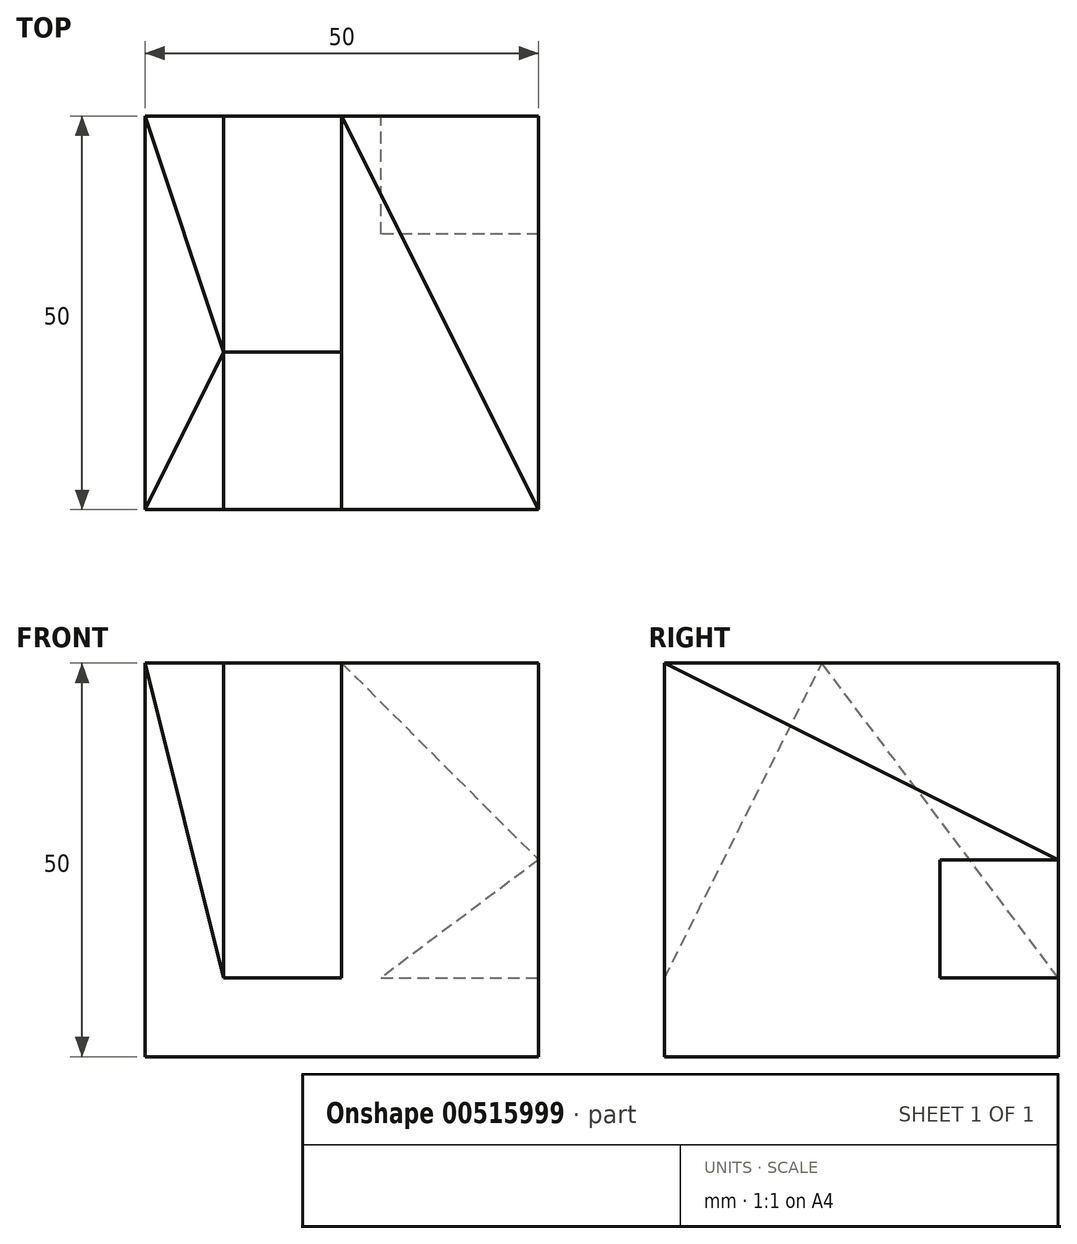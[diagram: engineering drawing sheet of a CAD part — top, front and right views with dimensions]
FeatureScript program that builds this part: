
annotation { "Feature Type Name" : "Feature", "Feature Type Description" : "" }
export const myFeature = defineFeature(function(context is Context, id is Id, definition is map)
    precondition{}
    {
        {
            var Q0;
            Q0=qCreatedBy(makeId("Front.planeOp"),FACE);
            var sketch = newSketch(context, id + "F0", { "sketchPlane" : qUnion([Q0])});
            skLineSegment(sketch, "E0.bottom", {"start": v(0, 0) * mm, "end": v(50, 0) * mm});
            skLineSegment(sketch, "E0.top", {"start": v(0, 50) * mm, "end": v(50, 50) * mm});
            skLineSegment(sketch, "E0.left", {"start": v(0, 0) * mm, "end": v(0, 50) * mm});
            skLineSegment(sketch, "E0.right", {"start": v(50, 0) * mm, "end": v(50, 50) * mm});
            skSolve(sketch);
        }
        {
            var Q0;
            Q0 = qSketchRegion(id + "F0", true);
            extrude(context, id + "F1", {"entities" : qUnion([Q0]), "depth" : 50 * mm, "offsetDistance" : 25 * mm});
        }
        {
            var Q0;
            Q0=makeQuery(id+"F1.opExtrude","SWEPT_FACE",FACE,{"disambiguationData":[OSD([sQuery(id+"F0.wireOp",EDGE,"E0.right")])]});
            var sketch = newSketch(context, id + "F2", { "sketchPlane" : qUnion([Q0])});
            skLineSegment(sketch, "E1", {"start": v(-30, 50) * mm, "end": v(-50, 10) * mm});
            skSolve(sketch);
        }
        {
            var Q0;
            {var subQ3=sQuery(id+"F2.wireOp",EDGE,"E1");Q0=makeQuery(id+"F2.imprint","IMPRINT",FACE,{"disambiguationData":[TD([[makeQuery(id+"F2.imprint","IMPRINT",EDGE,{"derivedFrom":subQ3}),1.0]])]});}
            var sketch = newSketch(context, id + "F3", { "sketchPlane" : qUnion([Q0])});
            skLineSegment(sketch, "E2", {"start": v(-30, 50) * mm, "end": v(0, 10) * mm});
            skSolve(sketch);
        }
        {
            var Q0;
            Q0=makeQuery(id+"F1.opExtrude","SWEPT_FACE",FACE,{"disambiguationData":[OSD([sQuery(id+"F0.wireOp",EDGE,"E0.top")])]});
            var sketch = newSketch(context, id + "F4", { "sketchPlane" : qUnion([Q0])});
            skLineSegment(sketch, "E3", {"start": v(50, -50) * mm, "end": v(25, 0) * mm});
            skSolve(sketch);
        }
        {
            var Q0;
            Q0=makeQuery(id+"F1.opExtrude","SWEPT_FACE",FACE,{"disambiguationData":[OSD([sQuery(id+"F0.wireOp",EDGE,"E0.right")])]});
            var sketch = newSketch(context, id + "F5", { "sketchPlane" : qUnion([Q0])});
            skLineSegment(sketch, "E4", {"start": v(-50, 50) * mm, "end": v(0, 25) * mm});
            skSolve(sketch);
        }
        {
            var Q0;
            Q0=makeQuery(id+"F1.opExtrude","CAP_FACE",FACE,{"disambiguationData":[OSD([sQuery(id+"F0.wireOp",EDGE,"E0.bottom"),sQuery(id+"F0.wireOp",EDGE,"E0.top"),sQuery(id+"F0.wireOp",EDGE,"E0.left"),sQuery(id+"F0.wireOp",EDGE,"E0.right")])],"isStart":true});
            var sketch = newSketch(context, id + "F6", { "sketchPlane" : qUnion([Q0])});
            skLineSegment(sketch, "E5", {"start": v(-25, 50) * mm, "end": v(-50, 25) * mm});
            skSolve(sketch);
        }
        {
            var Q0;
            {var subQ0=sQuery(id+"F6.wireOp",EDGE,"E5");Q0=makeQuery(id+"F6.imprint","IMPRINT",FACE,{"disambiguationData":[TD([[makeQuery(id+"F6.imprint","IMPRINT",EDGE,{"derivedFrom":subQ0}),-1.0]])]});}
            var Q1;
            Q1=sQuery(id+"F5.wireOp",EDGE,"E4");
            sweep(context, id + "F7", {"operationType" : NewBodyOperationType.REMOVE, "profiles" : qUnion([Q0]), "path" : qUnion([Q1])});
        }
        {
            var Q0;
            Q0=makeQuery(id+"F1.opExtrude","CAP_FACE",FACE,{"disambiguationData":[OSD([sQuery(id+"F0.wireOp",EDGE,"E0.bottom"),sQuery(id+"F0.wireOp",EDGE,"E0.top"),sQuery(id+"F0.wireOp",EDGE,"E0.left"),sQuery(id+"F0.wireOp",EDGE,"E0.right")])],"isStart":false});
            var sketch = newSketch(context, id + "F8", { "sketchPlane" : qUnion([Q0])});
            skLineSegment(sketch, "E6.bottom", {"start": v(10, 50) * mm, "end": v(25, 50) * mm});
            skLineSegment(sketch, "E6.top", {"start": v(10, 10) * mm, "end": v(25, 10) * mm});
            skLineSegment(sketch, "E6.left", {"start": v(10, 50) * mm, "end": v(10, 10) * mm});
            skLineSegment(sketch, "E6.right", {"start": v(25, 50) * mm, "end": v(25, 10) * mm});
            skSolve(sketch);
        }
        {
            var Q0;
            Q0=makeQuery(id+"F8.imprint","IMPRINT",FACE,{"disambiguationData":[TD([[makeQuery(id+"F8.imprint","IMPRINT",EDGE,{"derivedFrom":sQuery(id+"F8.wireOp",EDGE,"E6.bottom")}),-1.0]])]});
            var Q1;
            Q1=sQuery(id+"F2.wireOp",EDGE,"E1");
            sweep(context, id + "F9", {"operationType" : NewBodyOperationType.REMOVE, "profiles" : qUnion([Q0]), "path" : qUnion([Q1])});
        }
        {
            var Q0;
            Q0=makeQuery(id+"F1.opExtrude","CAP_FACE",FACE,{"disambiguationData":[OSD([sQuery(id+"F0.wireOp",EDGE,"E0.bottom"),sQuery(id+"F0.wireOp",EDGE,"E0.top"),sQuery(id+"F0.wireOp",EDGE,"E0.left"),sQuery(id+"F0.wireOp",EDGE,"E0.right")])],"isStart":true});
            var sketch = newSketch(context, id + "F10", { "sketchPlane" : qUnion([Q0])});
            skLineSegment(sketch, "E7.bottom", {"start": v(-25, 50) * mm, "end": v(-10, 50) * mm});
            skLineSegment(sketch, "E7.top", {"start": v(-25, 10) * mm, "end": v(-10, 10) * mm});
            skLineSegment(sketch, "E7.left", {"start": v(-25, 50) * mm, "end": v(-25, 10) * mm});
            skLineSegment(sketch, "E7.right", {"start": v(-10, 50) * mm, "end": v(-10, 10) * mm});
            skSolve(sketch);
        }
        {
            var Q0;
            Q0=makeQuery(id+"F10.imprint","IMPRINT",FACE,{"disambiguationData":[TD([[makeQuery(id+"F10.imprint","IMPRINT",EDGE,{"derivedFrom":sQuery(id+"F10.wireOp",EDGE,"E7.bottom")}),1.0]])]});
            var Q1;
            Q1=sQuery(id+"F3.wireOp",EDGE,"E2");
            sweep(context, id + "F11", {"operationType" : NewBodyOperationType.REMOVE, "profiles" : qUnion([Q0]), "path" : qUnion([Q1])});
        }
        {
            var Q0;
            Q0=makeQuery(id+"F1.opExtrude","CAP_FACE",FACE,{"disambiguationData":[OSD([sQuery(id+"F0.wireOp",EDGE,"E0.bottom"),sQuery(id+"F0.wireOp",EDGE,"E0.top"),sQuery(id+"F0.wireOp",EDGE,"E0.left"),sQuery(id+"F0.wireOp",EDGE,"E0.right")])],"isStart":false});
            var sketch = newSketch(context, id + "F12", { "sketchPlane" : qUnion([Q0])});
            skLineSegment(sketch, "E8", {"start": v(0, 50) * mm, "end": v(10, 10) * mm});
            skSolve(sketch);
        }
        {
            var Q0;
            {var subQ0=sQuery(id+"F4.wireOp",EDGE,"E3");Q0=makeQuery(id+"F4.imprint","IMPRINT",FACE,{"disambiguationData":[TD([[makeQuery(id+"F4.imprint","IMPRINT",EDGE,{"derivedFrom":subQ0}),1.0]])]});}
            var sketch = newSketch(context, id + "F13", { "sketchPlane" : qUnion([Q0])});
            skLineSegment(sketch, "E9", {"start": v(0, -49.98) * mm, "end": v(9.98, -30.01) * mm});
            skSolve(sketch);
        }
        {
            var Q0;
            Q0=makeQuery(id+"F9.boolean.opBoolean","COPY",FACE,{"derivedFrom":makeQuery(id+"F9.opSweep","SWEPT_FACE",FACE,{"disambiguationData":[OSD([sQuery(id+"F2.wireOp",EDGE,"E1"),sQuery(id+"F8.wireOp",EDGE,"E6.left")])]})});
            var Q1;
            Q1=sQuery(id+"F12.wireOp",EDGE,"E8");
            sweep(context, id + "F14", {"operationType" : NewBodyOperationType.REMOVE, "profiles" : qUnion([Q0]), "path" : qUnion([Q1])});
        }
        {
            var Q0;
            Q0=makeQuery(id+"F1.opExtrude","CAP_FACE",FACE,{"disambiguationData":[OSD([sQuery(id+"F0.wireOp",EDGE,"E0.bottom"),sQuery(id+"F0.wireOp",EDGE,"E0.top"),sQuery(id+"F0.wireOp",EDGE,"E0.left"),sQuery(id+"F0.wireOp",EDGE,"E0.right")])],"isStart":true});
            var sketch = newSketch(context, id + "F15", { "sketchPlane" : qUnion([Q0])});
            skLineSegment(sketch, "E10", {"start": v(0, 50) * mm, "end": v(-10, 10) * mm});
            skSolve(sketch);
        }
        {
            var Q0;
            Q0=makeQuery(id+"F11.boolean.opBoolean","COPY",FACE,{"derivedFrom":makeQuery(id+"F11.opSweep","SWEPT_FACE",FACE,{"disambiguationData":[OSD([sQuery(id+"F3.wireOp",EDGE,"E2"),sQuery(id+"F10.wireOp",EDGE,"E7.right")])]})});
            var Q1;
            Q1=sQuery(id+"F15.wireOp",EDGE,"E10");
            sweep(context, id + "F16", {"operationType" : NewBodyOperationType.REMOVE, "profiles" : qUnion([Q0]), "path" : qUnion([Q1])});
        }
        {
            var Q0;
            Q0=makeQuery(id+"F1.opExtrude","SWEPT_FACE",FACE,{"disambiguationData":[OSD([sQuery(id+"F0.wireOp",EDGE,"E0.right")])]});
            var sketch = newSketch(context, id + "F17", { "sketchPlane" : qUnion([Q0])});
            skLineSegment(sketch, "E11.bottom", {"start": v(0, 25) * mm, "end": v(-15, 25) * mm});
            skLineSegment(sketch, "E11.top", {"start": v(0, 10) * mm, "end": v(-15, 10) * mm});
            skLineSegment(sketch, "E11.left", {"start": v(0, 25) * mm, "end": v(0, 10) * mm});
            skLineSegment(sketch, "E11.right", {"start": v(-15, 25) * mm, "end": v(-15, 10) * mm});
            skSolve(sketch);
        }
        {
            var Q0;
            Q0=makeQuery(id+"F1.opExtrude","CAP_FACE",FACE,{"disambiguationData":[OSD([sQuery(id+"F0.wireOp",EDGE,"E0.bottom"),sQuery(id+"F0.wireOp",EDGE,"E0.top"),sQuery(id+"F0.wireOp",EDGE,"E0.left"),sQuery(id+"F0.wireOp",EDGE,"E0.right")])],"isStart":true});
            var sketch = newSketch(context, id + "F18", { "sketchPlane" : qUnion([Q0])});
            skLineSegment(sketch, "E12", {"start": v(-50, 25) * mm, "end": v(-30, 10) * mm});
            skLineSegment(sketch, "E13", {"start": v(-30, 10) * mm, "end": v(-50, 10) * mm});
            skSolve(sketch);
        }
        {
            var Q0;
            {var subQ0=sQuery(id+"F18.wireOp",EDGE,"E12");Q0=makeQuery(id+"F18.imprint","IMPRINT",FACE,{"disambiguationData":[TD([[makeQuery(id+"F18.imprint","IMPRINT",EDGE,{"derivedFrom":subQ0}),-1.0]])]});}
            var Q1;
            Q1=sQuery(id+"F17.wireOp",VERTEX,"E11.right.start");
            extrude(context, id + "F19", {"entities" : qUnion([Q0]), "operationType" : NewBodyOperationType.REMOVE, "endBound" : BoundingType.UP_TO_VERTEX, "oppositeDirection" : true, "depth" : 25 * mm, "endBoundEntityVertex" : qUnion([Q1]), "offsetDistance" : 25 * mm});
        }
    });
